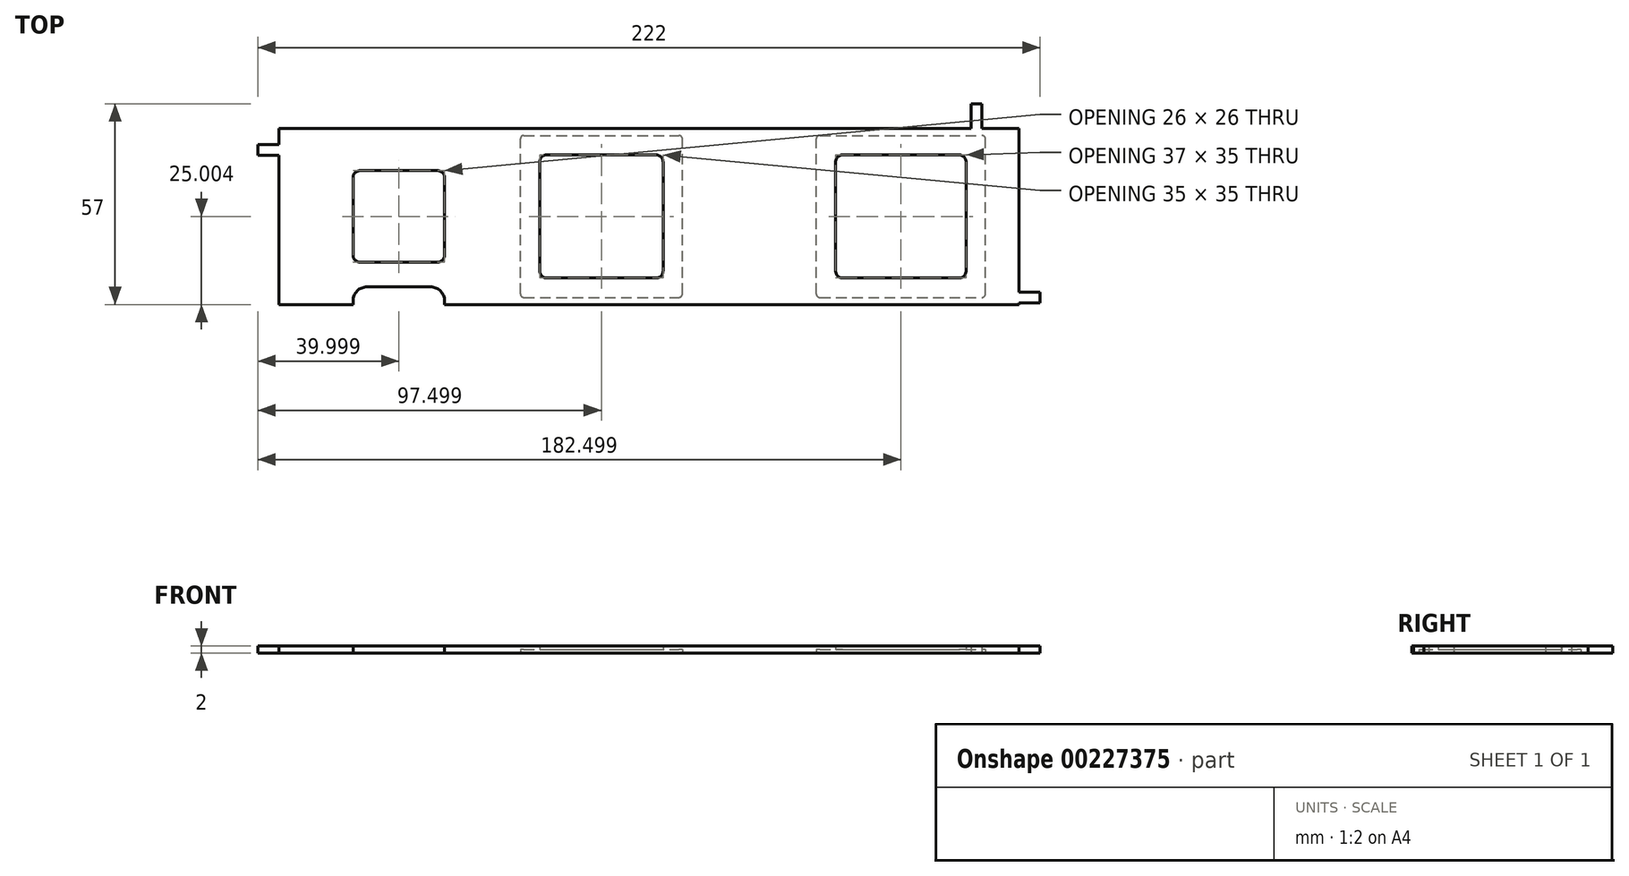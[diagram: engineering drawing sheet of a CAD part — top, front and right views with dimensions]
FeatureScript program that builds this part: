
annotation { "Feature Type Name" : "Feature", "Feature Type Description" : "" }
export const myFeature = defineFeature(function(context is Context, id is Id, definition is map)
    precondition{}
    {
        {
            var Q0;
            Q0=qCreatedBy(makeId("Top.planeOp"),FACE);
            var sketch = newSketch(context, id + "F0", { "sketchPlane" : qUnion([Q0])});
            skLineSegment(sketch, "E0.bottom", {"start": v(-22.9, 18.14) * mm, "end": v(187.1, 18.14) * mm});
            skLineSegment(sketch, "E0.top", {"start": v(-22.9, -31.86) * mm, "end": v(187.1, -31.86) * mm});
            skLineSegment(sketch, "E0.left", {"start": v(-22.9, 18.14) * mm, "end": v(-22.9, -31.86) * mm});
            skLineSegment(sketch, "E0.right", {"start": v(187.1, 18.14) * mm, "end": v(187.1, -31.86) * mm});
            skPoint(sketch, "E1.oppositeSnap0", {"position": v(-25.4, 18.14) * mm});
            skLineSegment(sketch, "E1.bottom", {"start": v(173.54, 25.14) * mm, "end": v(176.54, 25.14) * mm});
            skLineSegment(sketch, "E1.top", {"start": v(173.54, 18.14) * mm, "end": v(176.54, 18.14) * mm});
            skLineSegment(sketch, "E1.left", {"start": v(173.54, 25.14) * mm, "end": v(173.54, 18.14) * mm});
            skLineSegment(sketch, "E1.right", {"start": v(176.54, 25.14) * mm, "end": v(176.54, 18.14) * mm});
            skLineSegment(sketch, "E2.bottom", {"start": v(-8.51, -31.86) * mm, "end": v(-5.51, -31.86) * mm});
            skLineSegment(sketch, "E2.top", {"start": v(-8.51, -38.86) * mm, "end": v(-5.51, -38.86) * mm});
            skLineSegment(sketch, "E2.left", {"start": v(-8.51, -31.86) * mm, "end": v(-8.51, -38.86) * mm});
            skLineSegment(sketch, "E2.right", {"start": v(-5.51, -31.86) * mm, "end": v(-5.51, -38.86) * mm});
            skLineSegment(sketch, "E3.bottom", {"start": v(187.1, -28.4) * mm, "end": v(193.1, -28.4) * mm});
            skLineSegment(sketch, "E3.top", {"start": v(187.1, -31.4) * mm, "end": v(193.1, -31.4) * mm});
            skLineSegment(sketch, "E3.left", {"start": v(187.1, -28.4) * mm, "end": v(187.1, -31.4) * mm});
            skLineSegment(sketch, "E3.right", {"start": v(193.1, -28.4) * mm, "end": v(193.1, -31.4) * mm});
            skLineSegment(sketch, "E4.bottom", {"start": v(-28.9, 10.54) * mm, "end": v(-22.9, 10.54) * mm});
            skLineSegment(sketch, "E4.top", {"start": v(-28.9, 13.54) * mm, "end": v(-22.9, 13.54) * mm});
            skLineSegment(sketch, "E4.left", {"start": v(-28.9, 10.54) * mm, "end": v(-28.9, 13.54) * mm});
            skLineSegment(sketch, "E4.right", {"start": v(-22.9, 10.54) * mm, "end": v(-22.9, 13.54) * mm});
            skSolve(sketch);
        }
        {
            var Q0;
            Q0=makeQuery(id+"F0.imprint","IMPRINT",FACE,{"disambiguationData":[TD([[makeQuery(id+"F0.imprint","IMPRINT",EDGE,{"derivedFrom":sQuery(id+"F0.wireOp",EDGE,"E0.bottom")}),-1.0]])]});
            extrude(context, id + "F1", {"entities" : qUnion([Q0]), "depth" : 2 * mm});
        }
        {
            var Q0;
            Q0=makeQuery(id+"F1.opExtrude","CAP_FACE",FACE,{"disambiguationData":[OSD([sQuery(id+"F0.wireOp",EDGE,"E0.bottom"),sQuery(id+"F0.wireOp",EDGE,"E0.top"),sQuery(id+"F0.wireOp",EDGE,"E0.left"),sQuery(id+"F0.wireOp",EDGE,"E0.right")])],"isStart":true});
            var sketch = newSketch(context, id + "F2", { "sketchPlane" : qUnion([Q0])});
            skLineSegment(sketch, "E5.bottom", {"start": v(-1.9, 19.86) * mm, "end": v(24.1, 19.86) * mm});
            skLineSegment(sketch, "E5.top", {"start": v(-1.9, -6.14) * mm, "end": v(24.1, -6.14) * mm});
            skLineSegment(sketch, "E5.left", {"start": v(-1.9, 19.86) * mm, "end": v(-1.9, -6.14) * mm});
            skLineSegment(sketch, "E5.right", {"start": v(24.1, 19.86) * mm, "end": v(24.1, -6.14) * mm});
            skSolve(sketch);
        }
        {
            var Q0;
            Q0=makeQuery(id+"F2.imprint","IMPRINT",FACE,{"disambiguationData":[TD([[makeQuery(id+"F2.imprint","IMPRINT",EDGE,{"derivedFrom":sQuery(id+"F2.wireOp",EDGE,"E5.bottom")}),-1.0]])]});
            extrude(context, id + "F3", {"entities" : qUnion([Q0]), "operationType" : NewBodyOperationType.REMOVE, "oppositeDirection" : true, "depth" : 15.4 * mm});
        }
        {
            var Q0;
            Q0=makeQuery(id+"F1.opExtrude","CAP_FACE",FACE,{"disambiguationData":[OSD([sQuery(id+"F0.wireOp",EDGE,"E0.bottom"),sQuery(id+"F0.wireOp",EDGE,"E0.top"),sQuery(id+"F0.wireOp",EDGE,"E0.left"),sQuery(id+"F0.wireOp",EDGE,"E0.right")])],"isStart":true});
            var sketch = newSketch(context, id + "F4", { "sketchPlane" : qUnion([Q0])});
            skLineSegment(sketch, "E6.bottom", {"start": v(51.1, 24.36) * mm, "end": v(86.1, 24.36) * mm});
            skLineSegment(sketch, "E6.top", {"start": v(51.1, -10.64) * mm, "end": v(86.1, -10.64) * mm});
            skLineSegment(sketch, "E6.left", {"start": v(51.1, 24.36) * mm, "end": v(51.1, -10.64) * mm});
            skLineSegment(sketch, "E6.right", {"start": v(86.1, 24.36) * mm, "end": v(86.1, -10.64) * mm});
            skLineSegment(sketch, "E7.bottom", {"start": v(135.1, 24.36) * mm, "end": v(172.1, 24.36) * mm});
            skLineSegment(sketch, "E7.top", {"start": v(135.1, -10.64) * mm, "end": v(172.1, -10.64) * mm});
            skLineSegment(sketch, "E7.left", {"start": v(135.1, 24.36) * mm, "end": v(135.1, -10.64) * mm});
            skLineSegment(sketch, "E7.right", {"start": v(172.1, 24.36) * mm, "end": v(172.1, -10.64) * mm});
            skSolve(sketch);
        }
        {
            var Q0;
            Q0=makeQuery(id+"F4.imprint","IMPRINT",FACE,{"disambiguationData":[TD([[makeQuery(id+"F4.imprint","IMPRINT",EDGE,{"derivedFrom":sQuery(id+"F4.wireOp",EDGE,"E6.bottom")}),-1.0]])]});
            var Q1;
            Q1=makeQuery(id+"F4.imprint","IMPRINT",FACE,{"disambiguationData":[TD([[makeQuery(id+"F4.imprint","IMPRINT",EDGE,{"derivedFrom":sQuery(id+"F4.wireOp",EDGE,"E7.bottom")}),-1.0]])]});
            extrude(context, id + "F5", {"entities" : qUnion([Q0, Q1]), "operationType" : NewBodyOperationType.REMOVE, "oppositeDirection" : true, "depth" : 25 * mm});
        }
        {
            var Q0;
            Q0=makeQuery(id+"F1.opExtrude","CAP_FACE",FACE,{"disambiguationData":[OSD([sQuery(id+"F0.wireOp",EDGE,"E0.bottom"),sQuery(id+"F0.wireOp",EDGE,"E0.top"),sQuery(id+"F0.wireOp",EDGE,"E0.left"),sQuery(id+"F0.wireOp",EDGE,"E0.right")])],"isStart":false});
            var sketch = newSketch(context, id + "F6", { "sketchPlane" : qUnion([Q0])});
            skLineSegment(sketch, "E8.bottom", {"start": v(-1.9, -26.86) * mm, "end": v(24.1, -26.86) * mm});
            skLineSegment(sketch, "E8.top", {"start": v(-1.9, -31.86) * mm, "end": v(24.1, -31.86) * mm});
            skLineSegment(sketch, "E8.left", {"start": v(-1.9, -26.86) * mm, "end": v(-1.9, -31.86) * mm});
            skLineSegment(sketch, "E8.right", {"start": v(24.1, -26.86) * mm, "end": v(24.1, -31.86) * mm});
            skSolve(sketch);
        }
        {
            var Q0;
            Q0=makeQuery(id+"F6.imprint","IMPRINT",FACE,{"disambiguationData":[TD([[makeQuery(id+"F6.imprint","IMPRINT",EDGE,{"derivedFrom":sQuery(id+"F6.wireOp",EDGE,"E8.bottom")}),-1.0]])]});
            extrude(context, id + "F7", {"entities" : qUnion([Q0]), "operationType" : NewBodyOperationType.REMOVE, "oppositeDirection" : true, "depth" : 25 * mm});
        }
        {
            var Q0;
            Q0=makeQuery(id+"F7.boolean.opBoolean","COPY",EDGE,{"derivedFrom":makeQuery(id+"F7.opExtrude","SWEPT_EDGE",EDGE,{"disambiguationData":[OSD([sQuery(id+"F6.wireOp",EDGE,"E8.bottom"),sQuery(id+"F6.wireOp",EDGE,"E8.left")])]})});
            var Q1;
            Q1=makeQuery(id+"F7.boolean.opBoolean","COPY",EDGE,{"derivedFrom":makeQuery(id+"F7.opExtrude","SWEPT_EDGE",EDGE,{"disambiguationData":[OSD([sQuery(id+"F6.wireOp",EDGE,"E8.bottom"),sQuery(id+"F6.wireOp",EDGE,"E8.right")])]})});
            fillet(context, id + "F8", {"entities" : qUnion([Q0, Q1]), "radius" : 4 * mm, "tangentPropagation" : true, "allowEdgeOverflow" : false});
        }
        {
            var Q0;
            Q0=makeQuery(id+"F5.boolean.opBoolean","COPY",EDGE,{"derivedFrom":makeQuery(id+"F5.opExtrude","SWEPT_EDGE",EDGE,{"disambiguationData":[OSD([sQuery(id+"F4.wireOp",EDGE,"E6.top"),sQuery(id+"F4.wireOp",EDGE,"E6.left")])]})});
            var Q1;
            Q1=makeQuery(id+"F5.boolean.opBoolean","COPY",EDGE,{"derivedFrom":makeQuery(id+"F5.opExtrude","SWEPT_EDGE",EDGE,{"disambiguationData":[OSD([sQuery(id+"F4.wireOp",EDGE,"E6.top"),sQuery(id+"F4.wireOp",EDGE,"E6.right")])]})});
            var Q2;
            Q2=makeQuery(id+"F5.boolean.opBoolean","COPY",EDGE,{"derivedFrom":makeQuery(id+"F5.opExtrude","SWEPT_EDGE",EDGE,{"disambiguationData":[OSD([sQuery(id+"F4.wireOp",EDGE,"E6.bottom"),sQuery(id+"F4.wireOp",EDGE,"E6.left")])]})});
            var Q3;
            Q3=makeQuery(id+"F5.boolean.opBoolean","COPY",EDGE,{"derivedFrom":makeQuery(id+"F5.opExtrude","SWEPT_EDGE",EDGE,{"disambiguationData":[OSD([sQuery(id+"F4.wireOp",EDGE,"E7.bottom"),sQuery(id+"F4.wireOp",EDGE,"E7.left")])]})});
            var Q4;
            Q4=makeQuery(id+"F5.boolean.opBoolean","COPY",EDGE,{"derivedFrom":makeQuery(id+"F5.opExtrude","SWEPT_EDGE",EDGE,{"disambiguationData":[OSD([sQuery(id+"F4.wireOp",EDGE,"E6.bottom"),sQuery(id+"F4.wireOp",EDGE,"E6.right")])]})});
            var Q5;
            Q5=makeQuery(id+"F5.boolean.opBoolean","COPY",EDGE,{"derivedFrom":makeQuery(id+"F5.opExtrude","SWEPT_EDGE",EDGE,{"disambiguationData":[OSD([sQuery(id+"F4.wireOp",EDGE,"E7.bottom"),sQuery(id+"F4.wireOp",EDGE,"E7.right")])]})});
            var Q6;
            Q6=makeQuery(id+"F5.boolean.opBoolean","COPY",EDGE,{"derivedFrom":makeQuery(id+"F5.opExtrude","SWEPT_EDGE",EDGE,{"disambiguationData":[OSD([sQuery(id+"F4.wireOp",EDGE,"E7.top"),sQuery(id+"F4.wireOp",EDGE,"E7.left")])]})});
            var Q7;
            Q7=makeQuery(id+"F5.boolean.opBoolean","COPY",EDGE,{"derivedFrom":makeQuery(id+"F5.opExtrude","SWEPT_EDGE",EDGE,{"disambiguationData":[OSD([sQuery(id+"F4.wireOp",EDGE,"E7.top"),sQuery(id+"F4.wireOp",EDGE,"E7.right")])]})});
            var Q8;
            Q8=makeQuery(id+"F3.boolean.opBoolean","COPY",EDGE,{"derivedFrom":makeQuery(id+"F3.opExtrude","SWEPT_EDGE",EDGE,{"disambiguationData":[OSD([sQuery(id+"F2.wireOp",EDGE,"E5.top"),sQuery(id+"F2.wireOp",EDGE,"E5.right")])]})});
            var Q9;
            Q9=makeQuery(id+"F3.boolean.opBoolean","COPY",EDGE,{"derivedFrom":makeQuery(id+"F3.opExtrude","SWEPT_EDGE",EDGE,{"disambiguationData":[OSD([sQuery(id+"F2.wireOp",EDGE,"E5.top"),sQuery(id+"F2.wireOp",EDGE,"E5.left")])]})});
            var Q10;
            Q10=makeQuery(id+"F3.boolean.opBoolean","COPY",EDGE,{"derivedFrom":makeQuery(id+"F3.opExtrude","SWEPT_EDGE",EDGE,{"disambiguationData":[OSD([sQuery(id+"F2.wireOp",EDGE,"E5.bottom"),sQuery(id+"F2.wireOp",EDGE,"E5.right")])]})});
            var Q11;
            Q11=makeQuery(id+"F3.boolean.opBoolean","COPY",EDGE,{"derivedFrom":makeQuery(id+"F3.opExtrude","SWEPT_EDGE",EDGE,{"disambiguationData":[OSD([sQuery(id+"F2.wireOp",EDGE,"E5.bottom"),sQuery(id+"F2.wireOp",EDGE,"E5.left")])]})});
            fillet(context, id + "F9", {"entities" : qUnion([Q0, Q1, Q2, Q3, Q4, Q5, Q6, Q7, Q8, Q9, Q10, Q11]), "radius" : 2 * mm, "tangentPropagation" : true, "allowEdgeOverflow" : false});
        }
        {
            var Q0;
            Q0=makeQuery(id+"F0.imprint","IMPRINT",FACE,{"disambiguationData":[TD([[makeQuery(id+"F0.imprint","IMPRINT",EDGE,{"derivedFrom":sQuery(id+"F0.wireOp",EDGE,"E0.bottom")}),-1.0]])]});
            var sketch = newSketch(context, id + "F10", { "sketchPlane" : qUnion([Q0])});
            skLineSegment(sketch, "E9.bottom", {"start": v(45.6, -29.86) * mm, "end": v(91.6, -29.86) * mm});
            skLineSegment(sketch, "E9.top", {"start": v(45.6, 16.14) * mm, "end": v(91.6, 16.14) * mm});
            skLineSegment(sketch, "E9.left", {"start": v(45.6, -29.86) * mm, "end": v(45.6, 16.14) * mm});
            skLineSegment(sketch, "E9.right", {"start": v(91.6, -29.86) * mm, "end": v(91.6, 16.14) * mm});
            skLineSegment(sketch, "E10.bottom", {"start": v(129.6, -29.86) * mm, "end": v(177.6, -29.86) * mm});
            skLineSegment(sketch, "E10.top", {"start": v(129.6, 16.14) * mm, "end": v(177.6, 16.14) * mm});
            skLineSegment(sketch, "E10.left", {"start": v(129.6, -29.86) * mm, "end": v(129.6, 16.14) * mm});
            skLineSegment(sketch, "E10.right", {"start": v(177.6, -29.86) * mm, "end": v(177.6, 16.14) * mm});
            skSolve(sketch);
        }
        {
            var Q0;
            Q0=qSketchRegion(id+"F10",true);
            extrude(context, id + "F11", {"entities" : qUnion([Q0]), "operationType" : NewBodyOperationType.REMOVE, "depth" : 1 * mm});
        }
        {
            var Q0;
            Q0=makeQuery(id+"F11.boolean.opBoolean","COPY",EDGE,{"derivedFrom":makeQuery(id+"F11.opExtrude","SWEPT_EDGE",EDGE,{"disambiguationData":[OSD([sQuery(id+"F10.wireOp",EDGE,"E9.bottom"),sQuery(id+"F10.wireOp",EDGE,"E9.left")])]})});
            var Q1;
            Q1=makeQuery(id+"F11.boolean.opBoolean","COPY",EDGE,{"derivedFrom":makeQuery(id+"F11.opExtrude","SWEPT_EDGE",EDGE,{"disambiguationData":[OSD([sQuery(id+"F10.wireOp",EDGE,"E9.bottom"),sQuery(id+"F10.wireOp",EDGE,"E9.right")])]})});
            var Q2;
            Q2=makeQuery(id+"F11.boolean.opBoolean","COPY",EDGE,{"derivedFrom":makeQuery(id+"F11.opExtrude","SWEPT_EDGE",EDGE,{"disambiguationData":[OSD([sQuery(id+"F10.wireOp",EDGE,"E9.top"),sQuery(id+"F10.wireOp",EDGE,"E9.right")])]})});
            var Q3;
            Q3=makeQuery(id+"F11.boolean.opBoolean","COPY",EDGE,{"derivedFrom":makeQuery(id+"F11.opExtrude","SWEPT_EDGE",EDGE,{"disambiguationData":[OSD([sQuery(id+"F10.wireOp",EDGE,"E9.top"),sQuery(id+"F10.wireOp",EDGE,"E9.left")])]})});
            fillet(context, id + "F12", {"entities" : qUnion([Q0, Q1, Q2, Q3]), "radius" : 1 * mm, "tangentPropagation" : true, "allowEdgeOverflow" : false});
        }
        {
            var Q0;
            Q0=makeQuery(id+"F11.boolean.opBoolean","COPY",EDGE,{"derivedFrom":makeQuery(id+"F11.opExtrude","SWEPT_EDGE",EDGE,{"disambiguationData":[OSD([sQuery(id+"F10.wireOp",EDGE,"E10.bottom"),sQuery(id+"F10.wireOp",EDGE,"E10.left")])]})});
            var Q1;
            Q1=makeQuery(id+"F11.boolean.opBoolean","COPY",EDGE,{"derivedFrom":makeQuery(id+"F11.opExtrude","SWEPT_EDGE",EDGE,{"disambiguationData":[OSD([sQuery(id+"F10.wireOp",EDGE,"E10.bottom"),sQuery(id+"F10.wireOp",EDGE,"E10.right")])]})});
            var Q2;
            Q2=makeQuery(id+"F11.boolean.opBoolean","COPY",EDGE,{"derivedFrom":makeQuery(id+"F11.opExtrude","SWEPT_EDGE",EDGE,{"disambiguationData":[OSD([sQuery(id+"F10.wireOp",EDGE,"E10.top"),sQuery(id+"F10.wireOp",EDGE,"E10.right")])]})});
            var Q3;
            Q3=makeQuery(id+"F11.boolean.opBoolean","COPY",EDGE,{"derivedFrom":makeQuery(id+"F11.opExtrude","SWEPT_EDGE",EDGE,{"disambiguationData":[OSD([sQuery(id+"F10.wireOp",EDGE,"E10.top"),sQuery(id+"F10.wireOp",EDGE,"E10.left")])]})});
            fillet(context, id + "F13", {"entities" : qUnion([Q0, Q1, Q2, Q3]), "radius" : 1 * mm, "tangentPropagation" : true, "allowEdgeOverflow" : false});
        }
        {
            var Q0;
            Q0=makeQuery(id+"F0.imprint","IMPRINT",FACE,{"disambiguationData":[TD([[makeQuery(id+"F0.imprint","IMPRINT",EDGE,{"derivedFrom":sQuery(id+"F0.wireOp",EDGE,"E3.bottom")}),-1.0]])]});
            var Q1;
            Q1=makeQuery(id+"F0.imprint","IMPRINT",FACE,{"disambiguationData":[TD([[makeQuery(id+"F0.imprint","IMPRINT",EDGE,{"derivedFrom":sQuery(id+"F0.wireOp",EDGE,"E1.bottom")}),-1.0]])]});
            var Q2;
            Q2=makeQuery(id+"F0.imprint","IMPRINT",FACE,{"disambiguationData":[TD([[makeQuery(id+"F0.imprint","IMPRINT",EDGE,{"derivedFrom":sQuery(id+"F0.wireOp",EDGE,"gMm37RoQ-QMnn-3wSX-GLZN-vOBIeoNuV8F2.bottom")}),-1.0]])]});
            var Q3;
            Q3=makeQuery(id+"F0.imprint","IMPRINT",FACE,{"disambiguationData":[TD([[makeQuery(id+"F0.imprint","IMPRINT",EDGE,{"derivedFrom":sQuery(id+"F0.wireOp",EDGE,"E2.bottom")}),-1.0]])]});
            var Q4;
            Q4=makeQuery(id+"F0.imprint","IMPRINT",FACE,{"disambiguationData":[TD([[makeQuery(id+"F0.imprint","IMPRINT",EDGE,{"derivedFrom":sQuery(id+"F0.wireOp",EDGE,"E4.bottom")}),1.0]])]});
            extrude(context, id + "F14", {"entities" : qUnion([Q0, Q1, Q2, Q3, Q4]), "operationType" : NewBodyOperationType.ADD, "depth" : 2 * mm});
        }
    });
